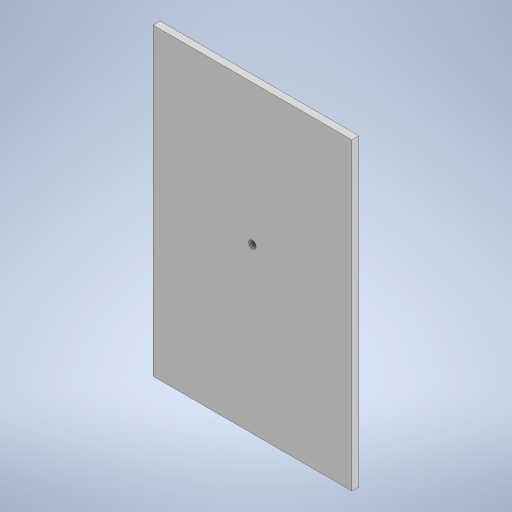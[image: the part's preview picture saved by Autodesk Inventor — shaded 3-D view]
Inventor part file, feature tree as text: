
AUTODESK INVENTOR PART (.ipt)
format: ipt  version: 2023 (Build 270158000, 158)  size: 210,432 bytes
history: native  units: mm
features: sketch x2, other x1, extrude x1, hole x1
ambient origin geometry x8: Origin, YZ Plane, XZ Plane, XY Plane, X Axis, Y Axis, Z Axis, Center Point
bodies: Body1 (feature_tree)
feature tree (5):
  other  "ソリッド1"
  extrude  "押し出し1"  Depth=85.0mm
  hole  "穴1"  [1 undecoded]
  sketch  "スケッチ1"
  sketch  "スケッチ2"
note: 1 required parameter value undecoded (feature->parameter linkage not recoverable at this tier; creation-order binding heuristic only, values carry confidence <= 0.55)
